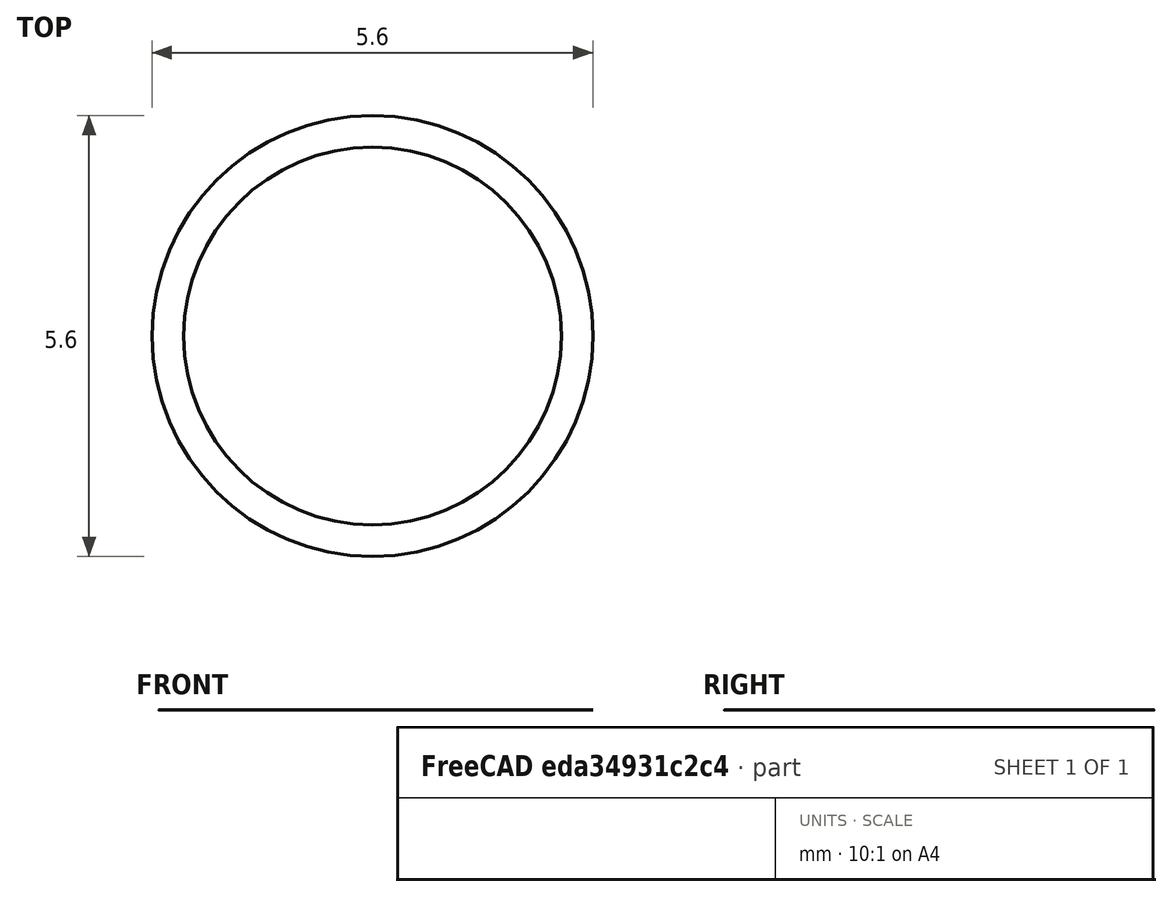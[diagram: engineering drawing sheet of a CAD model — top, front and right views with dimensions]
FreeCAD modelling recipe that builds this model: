
FCSTD DOCUMENT  (FreeCAD 1.0R39319 (Git))
Label: nested_coax
License: All rights reserved
LicenseURL: http://en.wikipedia.org/wiki/All_rights_reserved
objects: App::FeaturePython×5, Part::Part2DObjectPython×4, App::DocumentObjectGroupPython×3, Part::Cut×1
note: 5 computed .brp shape members not serialized (recipe doc carries the construction recipe); baked Part::Feature solids carry a one-line shape summary decoded from their .brp

FEATURE [Part::Part2DObjectPython] Circle001  # Draft 2D object (typed FeaturePython)
  Area = 24.6301
  FirstAngle = 0
  LastAngle = 0
  MakeFace = true
  Radius = 2.8
FEATURE [Part::Part2DObjectPython] Circle002  # Draft 2D object (typed FeaturePython)
  Area = 18.0956
  FirstAngle = 0
  LastAngle = 0
  MakeFace = true
  Radius = 2.4
FEATURE [App::FeaturePython] Dimension001  # Draft dimension (typed FeaturePython)
  Diameter = false
  Dimline = (1.8,4.6,0)
  Direction = (0,0,0)
  Distance = 4.8
  End = (2.4,1e-16,0)
  Normal = (0,0,-1)
  Start = (-2.4,-1e-16,0)
FEATURE [App::FeaturePython] Dimension002  # Draft dimension (typed FeaturePython)
  Diameter = false
  Dimline = (2.8,5,0)
  Direction = (0,0,0)
  Distance = 5.6
  End = (2.8,2e-16,0)
  Normal = (0,0,-1)
  Start = (-2.8,-2e-16,0)
FEATURE [App::FeaturePython] Dimension  # Draft dimension (typed FeaturePython)
  Diameter = false
  Dimline = (0.6,4.2,0)
  Direction = (0,0,0)
  Distance = 2
  End = (1,1e-16,0)
  Normal = (0,0,-1)
  Start = (-1,-1e-16,0)
FEATURE [App::FeaturePython] Dimension003  # Draft dimension (typed FeaturePython)
  Diameter = false
  Dimline = (3.6,5.4,0)
  Direction = (0,0,0)
  Distance = 8
  End = (-4,-2e-16,0)
  Normal = (0,0,-1)
  Start = (4,2e-16,0)
FEATURE [App::FeaturePython] PECMaterial  label="PEC"  # WARN: FeaturePython — macro-defined, semantics opaque (R4)
FEATURE [Part::Part2DObjectPython] Circle003  label="Conductor_2"  # Draft 2D object (typed FeaturePython)
  Area = 3.14159
  FirstAngle = 0
  LastAngle = 0
  MakeFace = true
  Material = -> PECMaterial
  Radius = 1
FEATURE [Part::Cut] Cut  label="Conductor_1"
  Base = -> Circle001
  Material = -> PECMaterial
  Tool = -> Circle002
FEATURE [Part::Part2DObjectPython] Circle004  label="ExtraConductor"  # Draft 2D object (typed FeaturePython)
  Area = 3.14159
  FirstAngle = 0
  LastAngle = 0
  MakeFace = true
  Material = -> PECMaterial
  Placement = pos=(5,0,0) rot=(0,0,1;0rad)
  Radius = 1
FEATURE [App::DocumentObjectGroupPython] MaterialGroup  label="Materials"  # scripted group (container) (typed FeaturePython)
  Group = -> [PECMaterial]
FEATURE [App::DocumentObjectGroupPython] CaseStudy  label="Model"  # scripted group (container) (typed FeaturePython)
  Group = -> [Cut,Circle003,Circle004]
FEATURE [App::DocumentObjectGroupPython] CrossSection  label="Cross-Section"  # scripted group (container) (typed FeaturePython)
  Group = -> [MaterialGroup,CaseStudy]
